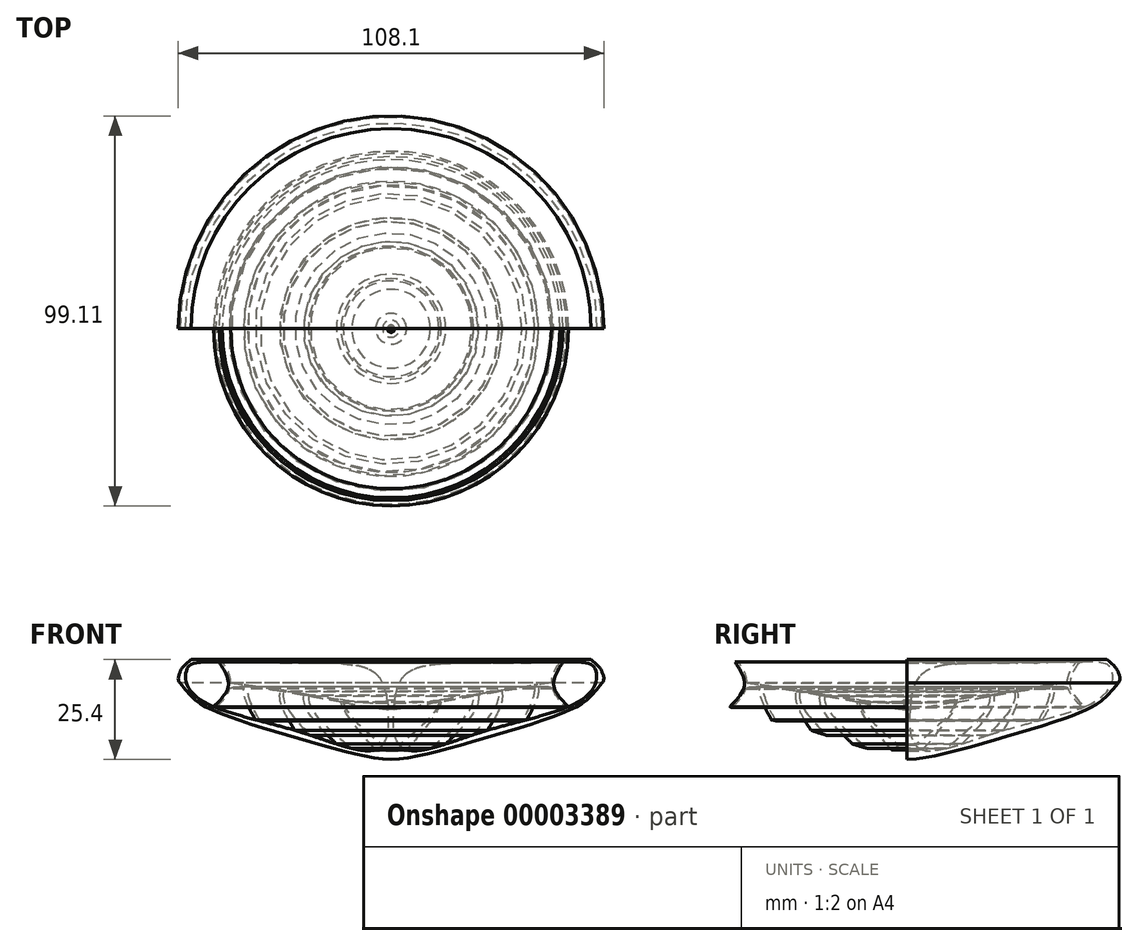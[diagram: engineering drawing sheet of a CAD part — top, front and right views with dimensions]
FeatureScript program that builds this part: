
annotation { "Feature Type Name" : "Feature", "Feature Type Description" : "" }
export const myFeature = defineFeature(function(context is Context, id is Id, definition is map)
    precondition{}
    {
        {
            var Q0;
            Q0=qCreatedBy(makeId("Front.planeOp"),FACE);
            var sketch = newSketch(context, id + "F0", { "sketchPlane" : qUnion([Q0])});
            skFitSpline(sketch, "E0", {"points": [v(-50.8, 0) * mm, v(-53.62, -3.23) * mm, v(-53.6, -5.93) * mm], "startDerivative": vector(-13.36, -11.27) * mm, "endDerivative": vector(5.53, -5.84) * mm});
            skFitSpline(sketch, "E1", {"points": [v(-53.6, -5.93) * mm, v(-46.03, -12.53) * mm, v(-21.33, -20.7) * mm, v(0, -25.4) * mm], "startDerivative": vector(34.96, -44.8) * mm, "endDerivative": vector(45.9, -1.7) * mm});
            skLineSegment(sketch, "E2", {"start": v(-50.8, 0) * mm, "end": v(0, 0) * mm});
            skLineSegment(sketch, "E3", {"start": v(0, 0) * mm, "end": v(0, -25.4) * mm});
            skFitSpline(sketch, "E4", {"points": [v(-50, -0.95) * mm, v(-51.73, -2.18) * mm, v(-52.14, -5.52) * mm, v(-47.08, -11) * mm, v(-22.46, -18.6) * mm, v(-2.9, -22.42) * mm, v(-0.79, -11.7) * mm, v(-4.4, -3.2) * mm, v(-18.46, -0.87) * mm, v(-34.69, -0.82) * mm, v(-50, -0.95) * mm]});
            skPoint(sketch, "E5.trimOffspring.end.orphan", {"position": v(-0.79, -11.6) * mm});
            skFitSpline(sketch, "E6", {"points": [v(-45.06, -11.97) * mm, v(-41.33, -6.48) * mm, v(-43.7, -0.61) * mm], "startDerivative": vector(10.11, 9.9) * mm, "endDerivative": vector(-7.7, 12.08) * mm});
            skFitSpline(sketch, "E7", {"points": [v(-42.93, -0.62) * mm, v(-40.78, -6.55) * mm, v(-44.54, -12.18) * mm], "startDerivative": vector(9.88, -12.33) * mm, "endDerivative": vector(-11.73, -10.95) * mm});
            skFitSpline(sketch, "E8", {"points": [v(-33.06, -0.85) * mm, v(-37.43, -6.8) * mm, v(-34.46, -15.29) * mm], "startDerivative": vector(-12.7, -11.81) * mm, "endDerivative": vector(9.57, -17.06) * mm});
            skFitSpline(sketch, "E9", {"points": [v(-32.14, -0.86) * mm, v(-36.39, -6.65) * mm, v(-33.3, -15.59) * mm], "startDerivative": vector(-12.56, -11.59) * mm, "endDerivative": vector(9.76, -17.84) * mm});
            skFitSpline(sketch, "E10", {"points": [v(-21.31, -0.86) * mm, v(-28.2, -8.33) * mm, v(-24.42, -18) * mm], "startDerivative": vector(-19.16, -13.87) * mm, "endDerivative": vector(12.84, -20.38) * mm});
            skFitSpline(sketch, "E11", {"points": [v(-20.55, -19.22) * mm, v(-27.39, -8.7) * mm, v(-19.56, -0.86) * mm], "startDerivative": vector(-20.78, 21.63) * mm, "endDerivative": vector(23.3, 15) * mm});
            skFitSpline(sketch, "E12", {"points": [v(-12.22, -1.08) * mm, v(-22.2, -9.28) * mm, v(-13.88, -21.45) * mm], "startDerivative": vector(-29.5, -15.35) * mm, "endDerivative": vector(25.6, -25.2) * mm});
            skFitSpline(sketch, "E13", {"points": [v(-9.98, -22.57) * mm, v(-20.95, -9.43) * mm, v(-9.84, -1.35) * mm], "startDerivative": vector(-32.47, 26.98) * mm, "endDerivative": vector(33.97, 15.22) * mm});
            skFitSpline(sketch, "E14", {"points": [v(-5.85, -2.4) * mm, v(-12.97, -8.55) * mm, v(-3.92, -22.9) * mm], "startDerivative": vector(-23.62, -12.1) * mm, "endDerivative": vector(25.1, -28.1) * mm});
            skFitSpline(sketch, "E15", {"points": [v(-3.16, -4.31) * mm, v(-12.17, -10.01) * mm, v(-2.14, -21.72) * mm], "startDerivative": vector(-28.5, -10.53) * mm, "endDerivative": vector(28.77, -23.87) * mm});
            skFitSpline(sketch, "E16", {"points": [v(-0.94, -10.38) * mm, v(-40.72, -5.9) * mm], "startDerivative": vector(-5.36, -7.23) * mm, "endDerivative": vector(-39.78, 4.48) * mm});
            skFitSpline(sketch, "E17", {"points": [v(-41, -7.48) * mm, v(-0.7, -12.72) * mm], "startDerivative": vector(4.2, 7.33) * mm, "endDerivative": vector(40.3, -5.24) * mm});
            skSolve(sketch);
        }
        {
            var Q0;
            Q0=makeQuery(id+"F0.imprint","IMPRINT",FACE,{"disambiguationData":[TD([[makeQuery(id+"F0.imprint","IMPRINT",EDGE,{"derivedFrom":sQuery(id+"F0.wireOp",EDGE,"E0")}),1.0]])]});
            var Q1;
            Q1=sQuery(id+"F0.wireOp",EDGE,"E3");
            revolve(context, id + "F1", {"entities" : qUnion([Q0]), "axis" : qUnion([Q1]), "revolveType" : RevolveType.ONE_DIRECTION, "angle" : 180 * degree});
        }
        {
            var Q0;
            {var subQ6=sQuery(id+"F0.wireOp",EDGE,"E6");Q0=makeQuery(id+"F0.imprint","IMPRINT",FACE,{"disambiguationData":[TD([[makeQuery(id+"F0.imprint","IMPRINT",EDGE,{"derivedFrom":subQ6}),-1.0]])]});}
            var Q1;
            {var subQ1=sQuery(id+"F0.wireOp",EDGE,"E17");Q1=makeQuery(id+"F0.imprint","IMPRINT",FACE,{"disambiguationData":[TD([[makeQuery(id+"F0.imprint","IMPRINT",EDGE,{"derivedFrom":subQ1}),1.0]])]});}
            var Q2;
            {var subQ1=sQuery(id+"F0.wireOp",EDGE,"E17");Q2=makeQuery(id+"F0.imprint","IMPRINT",FACE,{"disambiguationData":[TD([[makeQuery(id+"F0.imprint","IMPRINT",EDGE,{"derivedFrom":subQ1}),1.0]])]});}
            var Q3;
            {var subQ1=sQuery(id+"F0.wireOp",EDGE,"E17");Q3=makeQuery(id+"F0.imprint","IMPRINT",FACE,{"disambiguationData":[TD([[makeQuery(id+"F0.imprint","IMPRINT",EDGE,{"derivedFrom":subQ1}),1.0]])]});}
            var Q4;
            {var subQ1=sQuery(id+"F0.wireOp",EDGE,"E17");Q4=makeQuery(id+"F0.imprint","IMPRINT",FACE,{"disambiguationData":[TD([[makeQuery(id+"F0.imprint","IMPRINT",EDGE,{"derivedFrom":subQ1}),1.0]])]});}
            var Q5;
            {var subQ1=sQuery(id+"F0.wireOp",EDGE,"E16");Q5=makeQuery(id+"F0.imprint","IMPRINT",FACE,{"disambiguationData":[TD([[makeQuery(id+"F0.imprint","IMPRINT",EDGE,{"derivedFrom":subQ1}),1.0]])]});}
            var Q6;
            {var subQ3=sQuery(id+"F0.wireOp",EDGE,"E4");var subQ5=sQuery(id+"F0.wireOp",EDGE,"E14");var subQ7=makeQuery(id+"F0.imprint","INTERSECT",VERTEX,{"disambiguationData":[OD(1.0)],"derivedFrom":[subQ3,subQ5]});Q6=makeQuery(id+"F0.imprint","IMPRINT",FACE,{"disambiguationData":[TD([[makeQuery(id+"F0.imprint","IMPRINT",EDGE,{"disambiguationData":[TD([[subQ7,-1.0]])],"derivedFrom":subQ3}),1.0]])]});}
            var Q7;
            {var subQ2=sQuery(id+"F0.wireOp",EDGE,"E4");var subQ6=sQuery(id+"F0.wireOp",EDGE,"E12");var subQ8=makeQuery(id+"F0.imprint","INTERSECT",VERTEX,{"disambiguationData":[OD(1.0)],"derivedFrom":[subQ2,subQ6]});Q7=makeQuery(id+"F0.imprint","IMPRINT",FACE,{"disambiguationData":[TD([[makeQuery(id+"F0.imprint","IMPRINT",EDGE,{"disambiguationData":[TD([[subQ8,-1.0]])],"derivedFrom":subQ2}),1.0]])]});}
            var Q8;
            {var subQ2=sQuery(id+"F0.wireOp",EDGE,"E4");var subQ6=sQuery(id+"F0.wireOp",EDGE,"E10");var subQ8=makeQuery(id+"F0.imprint","INTERSECT",VERTEX,{"disambiguationData":[OD(1.0)],"derivedFrom":[subQ2,subQ6]});Q8=makeQuery(id+"F0.imprint","IMPRINT",FACE,{"disambiguationData":[TD([[makeQuery(id+"F0.imprint","IMPRINT",EDGE,{"disambiguationData":[TD([[subQ8,-1.0]])],"derivedFrom":subQ2}),1.0]])]});}
            var Q9;
            {var subQ2=sQuery(id+"F0.wireOp",EDGE,"E4");var subQ5=sQuery(id+"F0.wireOp",EDGE,"E8");var subQ7=makeQuery(id+"F0.imprint","INTERSECT",VERTEX,{"disambiguationData":[OD(1.0)],"derivedFrom":[subQ2,subQ5]});Q9=makeQuery(id+"F0.imprint","IMPRINT",FACE,{"disambiguationData":[TD([[makeQuery(id+"F0.imprint","IMPRINT",EDGE,{"disambiguationData":[TD([[subQ7,-1.0]])],"derivedFrom":subQ2}),1.0]])]});}
            var Q10;
            Q10=sQuery(id+"F0.wireOp",EDGE,"E3");
            revolve(context, id + "F2", {"entities" : qUnion([Q0, Q1, Q2, Q3, Q4, Q5, Q6, Q7, Q8, Q9]), "axis" : qUnion([Q10]), "revolveType" : RevolveType.FULL});
        }
    });
